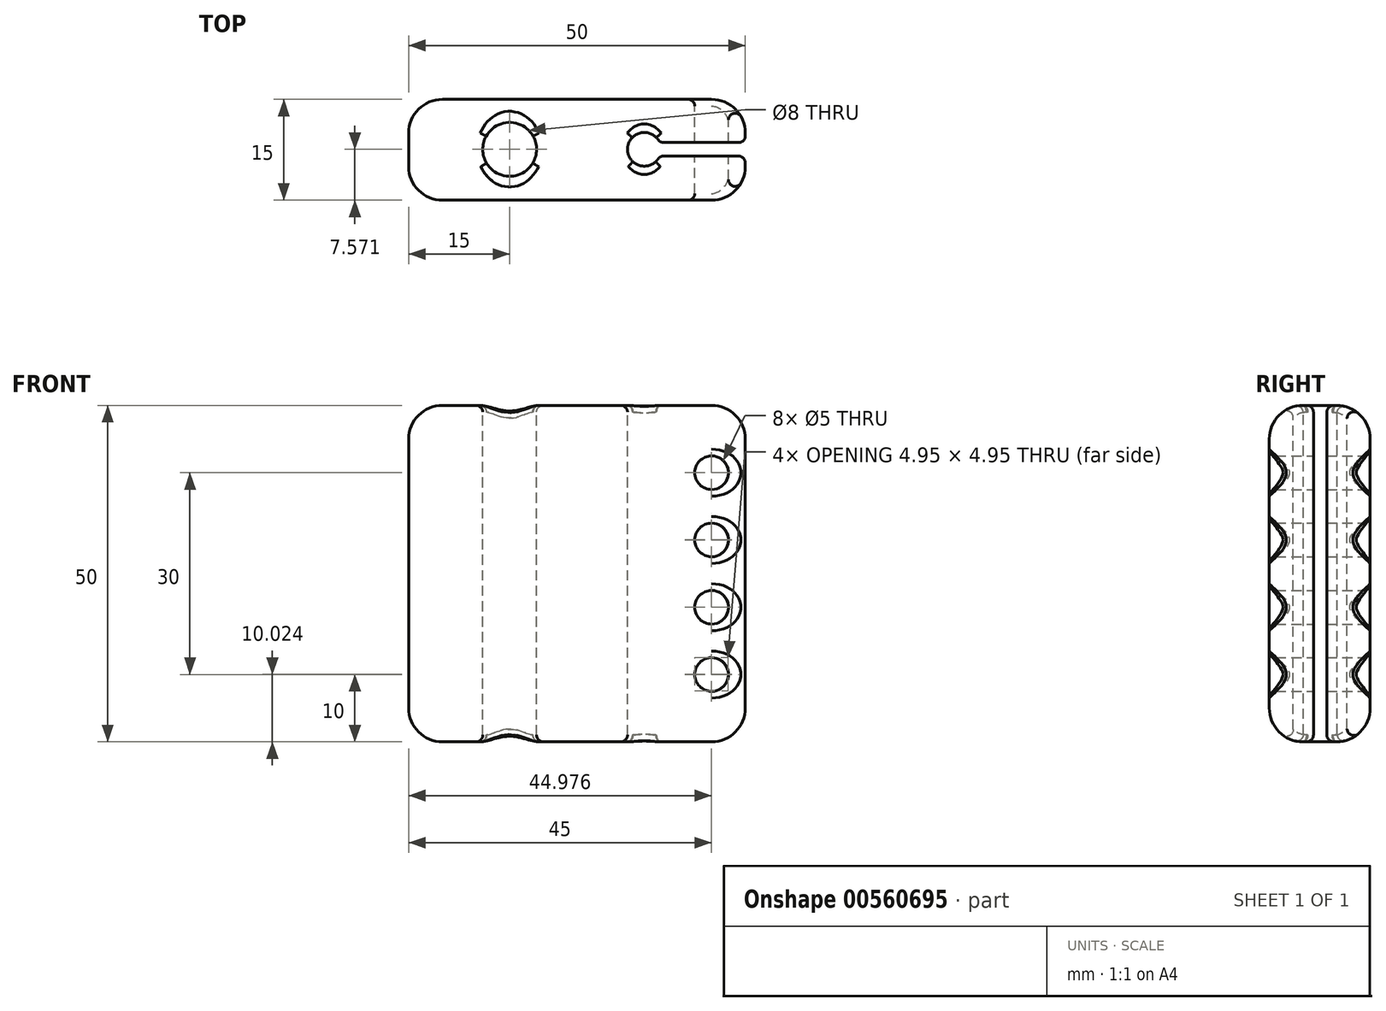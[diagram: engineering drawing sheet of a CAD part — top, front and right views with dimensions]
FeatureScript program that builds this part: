
annotation { "Feature Type Name" : "Feature", "Feature Type Description" : "" }
export const myFeature = defineFeature(function(context is Context, id is Id, definition is map)
    precondition{}
    {
        {
            var Q0;
            Q0=qCreatedBy(makeId("Front.planeOp"),FACE);
            var sketch = newSketch(context, id + "F0", { "sketchPlane" : qUnion([Q0])});
            skLineSegment(sketch, "E0.bottom", {"start": v(0, 0) * mm, "end": v(50, 0) * mm});
            skLineSegment(sketch, "E0.top", {"start": v(0, -50) * mm, "end": v(50, -50) * mm});
            skLineSegment(sketch, "E0.left", {"start": v(0, 0) * mm, "end": v(0, -50) * mm});
            skLineSegment(sketch, "E0.right", {"start": v(50, 0) * mm, "end": v(50, -50) * mm});
            skSolve(sketch);
        }
        {
            var Q0;
            Q0=makeQuery(id+"F0.imprint","IMPRINT",FACE,{"disambiguationData":[TD([[makeQuery(id+"F0.imprint","IMPRINT",EDGE,{"derivedFrom":sQuery(id+"F0.wireOp",EDGE,"E0.bottom")}),-1.0]])]});
            extrude(context, id + "F1", {"entities" : qUnion([Q0]), "depth" : 15 * mm, "offsetDistance" : 25 * mm});
        }
        {
            var Q0;
            Q0=qCreatedBy(makeId("Top.planeOp"),FACE);
            var sketch = newSketch(context, id + "F2", { "sketchPlane" : qUnion([Q0])});
            skCircle(sketch, "E1", {"center": v(35, -7.43) * mm, "radius": 2.5 * mm});
            skCircle(sketch, "E2", {"center": v(15, -7.43) * mm, "radius": 4 * mm});
            skLineSegment(sketch, "E3", {"start": v(37.5, -7.43) * mm, "end": v(68.19, -7.43) * mm, "construction": true});
            skLineSegment(sketch, "E4", {"start": v(55.03, -8.43) * mm, "end": v(55.03, -6.43) * mm});
            skLineSegment(sketch, "E5", {"start": v(55.03, -6.43) * mm, "end": v(37.3, -6.43) * mm});
            skLineSegment(sketch, "E6", {"start": v(55.03, -8.43) * mm, "end": v(37.3, -8.43) * mm});
            skSolve(sketch);
        }
        {
            var Q0;
            Q0=makeQuery(id+"F2.imprint","IMPRINT",FACE,{"disambiguationData":[TD([[makeQuery(id+"F2.imprint","IMPRINT",EDGE,{"derivedFrom":sQuery(id+"F2.wireOp",EDGE,"E1")}),1.0]])]});
            var Q1;
            Q1=makeQuery(id+"F2.imprint","IMPRINT",FACE,{"disambiguationData":[TD([[makeQuery(id+"F2.imprint","IMPRINT",EDGE,{"derivedFrom":sQuery(id+"F2.wireOp",EDGE,"E2")}),1.0]])]});
            var Q2;
            {var subQ5=sQuery(id+"F2.wireOp",EDGE,"E4");Q2=makeQuery(id+"F2.imprint","IMPRINT",FACE,{"disambiguationData":[TD([[makeQuery(id+"F2.imprint","IMPRINT",EDGE,{"derivedFrom":subQ5}),1.0]])]});}
            extrude(context, id + "F3", {"entities" : qUnion([Q0, Q1, Q2]), "operationType" : NewBodyOperationType.REMOVE, "endBound" : BoundingType.THROUGH_ALL, "oppositeDirection" : true, "depth" : 25 * mm, "offsetDistance" : 25 * mm});
        }
        {
            var Q0;
            Q0=qCreatedBy(makeId("Front.planeOp"),FACE);
            var sketch = newSketch(context, id + "F4", { "sketchPlane" : qUnion([Q0])});
            skCircle(sketch, "E7", {"center": v(45, -40) * mm, "radius": 2.5 * mm});
            skCircle(sketch, "E8", {"center": v(45, -30) * mm, "radius": 2.5 * mm});
            skCircle(sketch, "E9", {"center": v(45, -10) * mm, "radius": 2.5 * mm});
            skCircle(sketch, "E10", {"center": v(45, -20) * mm, "radius": 2.5 * mm});
            skSolve(sketch);
        }
        {
            var Q0;
            Q0 = qSketchRegion(id + "F4", true);
            extrude(context, id + "F5", {"entities" : qUnion([Q0]), "operationType" : NewBodyOperationType.REMOVE, "endBound" : BoundingType.THROUGH_ALL, "depth" : 25 * mm, "offsetDistance" : 25 * mm});
        }
        {
            var Q0;
            Q0=makeQuery(id+"F1.opExtrude","CAP_EDGE",EDGE,{"disambiguationData":[OSD([sQuery(id+"F0.wireOp",EDGE,"E0.right")])],"isStart":false});
            var Q1;
            Q1=makeQuery(id+"F1.opExtrude","CAP_EDGE",EDGE,{"disambiguationData":[OSD([sQuery(id+"F0.wireOp",EDGE,"E0.right")])],"isStart":true});
            var Q2;
            Q2=makeQuery(id+"F1.opExtrude","CAP_EDGE",EDGE,{"disambiguationData":[OSD([sQuery(id+"F0.wireOp",EDGE,"E0.left")])],"isStart":true});
            var Q3;
            Q3=makeQuery(id+"F1.opExtrude","CAP_EDGE",EDGE,{"disambiguationData":[OSD([sQuery(id+"F0.wireOp",EDGE,"E0.left")])],"isStart":false});
            var Q4;
            Q4=makeQuery(id+"F1.opExtrude","SWEPT_EDGE",EDGE,{"disambiguationData":[OSD([sQuery(id+"F0.wireOp",EDGE,"E0.top"),sQuery(id+"F0.wireOp",EDGE,"E0.left")])]});
            var Q5;
            {var subQ0=sQuery(id+"F0.wireOp",EDGE,"E0.right");var subQ1=sQuery(id+"F0.wireOp",EDGE,"E0.top");Q5=makeQuery(id+"F3.boolean.opBoolean","SPLIT",EDGE,{"disambiguationData":[TD([makeQuery(id+"F3.opExtrude","SWEPT_FACE",FACE,{"disambiguationData":[OSD([sQuery(id+"F2.wireOp",EDGE,"E5")])]})])],"derivedFrom":makeQuery(id+"F1.opExtrude","SWEPT_EDGE",EDGE,{"disambiguationData":[OSD([subQ1,subQ0])]})});}
            var Q6;
            {var subQ0=sQuery(id+"F0.wireOp",EDGE,"E0.right");var subQ1=sQuery(id+"F0.wireOp",EDGE,"E0.top");Q6=makeQuery(id+"F3.boolean.opBoolean","SPLIT",EDGE,{"disambiguationData":[TD([makeQuery(id+"F3.opExtrude","SWEPT_FACE",FACE,{"disambiguationData":[OSD([sQuery(id+"F2.wireOp",EDGE,"E6")])]})])],"derivedFrom":makeQuery(id+"F1.opExtrude","SWEPT_EDGE",EDGE,{"disambiguationData":[OSD([subQ1,subQ0])]})});}
            var Q7;
            Q7=makeQuery(id+"F1.opExtrude","SWEPT_EDGE",EDGE,{"disambiguationData":[OSD([sQuery(id+"F0.wireOp",EDGE,"E0.bottom"),sQuery(id+"F0.wireOp",EDGE,"E0.left")])]});
            var Q8;
            {var subQ0=sQuery(id+"F0.wireOp",EDGE,"E0.bottom");var subQ1=sQuery(id+"F0.wireOp",EDGE,"E0.right");Q8=makeQuery(id+"F3.boolean.opBoolean","SPLIT",EDGE,{"disambiguationData":[TD([makeQuery(id+"F3.opExtrude","SWEPT_FACE",FACE,{"disambiguationData":[OSD([sQuery(id+"F2.wireOp",EDGE,"E5")])]})])],"derivedFrom":makeQuery(id+"F1.opExtrude","SWEPT_EDGE",EDGE,{"disambiguationData":[OSD([subQ0,subQ1])]})});}
            var Q9;
            {var subQ0=sQuery(id+"F0.wireOp",EDGE,"E0.bottom");var subQ1=sQuery(id+"F0.wireOp",EDGE,"E0.right");Q9=makeQuery(id+"F3.boolean.opBoolean","SPLIT",EDGE,{"disambiguationData":[TD([makeQuery(id+"F3.opExtrude","SWEPT_FACE",FACE,{"disambiguationData":[OSD([sQuery(id+"F2.wireOp",EDGE,"E6")])]})])],"derivedFrom":makeQuery(id+"F1.opExtrude","SWEPT_EDGE",EDGE,{"disambiguationData":[OSD([subQ0,subQ1])]})});}
            var Q10;
            Q10=makeQuery(id+"F1.opExtrude","CAP_EDGE",EDGE,{"disambiguationData":[OSD([sQuery(id+"F0.wireOp",EDGE,"E0.top")])],"isStart":true});
            var Q11;
            Q11=makeQuery(id+"F1.opExtrude","CAP_EDGE",EDGE,{"disambiguationData":[OSD([sQuery(id+"F0.wireOp",EDGE,"E0.top")])],"isStart":false});
            var Q12;
            Q12=makeQuery(id+"F1.opExtrude","CAP_EDGE",EDGE,{"disambiguationData":[OSD([sQuery(id+"F0.wireOp",EDGE,"E0.bottom")])],"isStart":true});
            var Q13;
            Q13=makeQuery(id+"F1.opExtrude","CAP_EDGE",EDGE,{"disambiguationData":[OSD([sQuery(id+"F0.wireOp",EDGE,"E0.bottom")])],"isStart":false});
            fillet(context, id + "F6", {"entities" : qUnion([Q0, Q1, Q2, Q3, Q4, Q5, Q6, Q7, Q8, Q9, Q10, Q11, Q12, Q13]), "radius" : 5 * mm, "tangentPropagation" : true, "allowEdgeOverflow" : false});
        }
        {
            var Q0;
            {var subQ0=sQuery(id+"F0.wireOp",EDGE,"E0.right");Q0=makeQuery(id+"F6.opFillet","BLEND_EDGE",EDGE,{"blendedFrom":[makeQuery(id+"F1.opExtrude","CAP_EDGE",EDGE,{"disambiguationData":[OSD([subQ0])],"isStart":false}),makeQuery(id+"F5.boolean.opBoolean","COPY",FACE,{"disambiguationData":[TD([makeQuery(id+"F3.boolean.opBoolean","COPY",FACE,{"derivedFrom":makeQuery(id+"F3.opExtrude","SWEPT_FACE",FACE,{"disambiguationData":[OSD([sQuery(id+"F2.wireOp",EDGE,"E6")])]})})])],"derivedFrom":makeQuery(id+"F5.opExtrude","SWEPT_FACE",FACE,{"disambiguationData":[OSD([sQuery(id+"F4.wireOp",EDGE,"E9")])]})})],"blendedInto":[makeQuery(id+"F5.boolean.opBoolean","COPY",FACE,{"disambiguationData":[TD([makeQuery(id+"F3.boolean.opBoolean","COPY",FACE,{"derivedFrom":makeQuery(id+"F3.opExtrude","SWEPT_FACE",FACE,{"disambiguationData":[OSD([sQuery(id+"F2.wireOp",EDGE,"E6")])]})})])],"derivedFrom":makeQuery(id+"F5.opExtrude","SWEPT_FACE",FACE,{"disambiguationData":[OSD([sQuery(id+"F4.wireOp",EDGE,"E9")])]})})]});}
            var Q1;
            Q1=makeQuery(id+"F5.boolean.opBoolean","INTERSECT",EDGE,{"derivedFrom":[makeQuery(id+"F1.opExtrude","CAP_FACE",FACE,{"disambiguationData":[OSD([sQuery(id+"F0.wireOp",EDGE,"E0.bottom"),sQuery(id+"F0.wireOp",EDGE,"E0.top"),sQuery(id+"F0.wireOp",EDGE,"E0.left"),sQuery(id+"F0.wireOp",EDGE,"E0.right")])],"isStart":false}),makeQuery(id+"F5.opExtrude","SWEPT_FACE",FACE,{"disambiguationData":[OSD([sQuery(id+"F4.wireOp",EDGE,"E9")])]})]});
            var Q2;
            {var subQ0=sQuery(id+"F0.wireOp",EDGE,"E0.right");Q2=makeQuery(id+"F6.opFillet","BLEND_EDGE",EDGE,{"blendedFrom":[makeQuery(id+"F1.opExtrude","CAP_EDGE",EDGE,{"disambiguationData":[OSD([subQ0])],"isStart":false}),makeQuery(id+"F5.boolean.opBoolean","COPY",FACE,{"disambiguationData":[TD([makeQuery(id+"F3.boolean.opBoolean","COPY",FACE,{"derivedFrom":makeQuery(id+"F3.opExtrude","SWEPT_FACE",FACE,{"disambiguationData":[OSD([sQuery(id+"F2.wireOp",EDGE,"E6")])]})})])],"derivedFrom":makeQuery(id+"F5.opExtrude","SWEPT_FACE",FACE,{"disambiguationData":[OSD([sQuery(id+"F4.wireOp",EDGE,"E10")])]})})],"blendedInto":[makeQuery(id+"F5.boolean.opBoolean","COPY",FACE,{"disambiguationData":[TD([makeQuery(id+"F3.boolean.opBoolean","COPY",FACE,{"derivedFrom":makeQuery(id+"F3.opExtrude","SWEPT_FACE",FACE,{"disambiguationData":[OSD([sQuery(id+"F2.wireOp",EDGE,"E6")])]})})])],"derivedFrom":makeQuery(id+"F5.opExtrude","SWEPT_FACE",FACE,{"disambiguationData":[OSD([sQuery(id+"F4.wireOp",EDGE,"E10")])]})})]});}
            var Q3;
            {var subQ0=sQuery(id+"F0.wireOp",EDGE,"E0.right");Q3=makeQuery(id+"F6.opFillet","BLEND_EDGE",EDGE,{"blendedFrom":[makeQuery(id+"F1.opExtrude","CAP_EDGE",EDGE,{"disambiguationData":[OSD([subQ0])],"isStart":false}),makeQuery(id+"F5.boolean.opBoolean","COPY",FACE,{"disambiguationData":[TD([makeQuery(id+"F3.boolean.opBoolean","COPY",FACE,{"derivedFrom":makeQuery(id+"F3.opExtrude","SWEPT_FACE",FACE,{"disambiguationData":[OSD([sQuery(id+"F2.wireOp",EDGE,"E6")])]})})])],"derivedFrom":makeQuery(id+"F5.opExtrude","SWEPT_FACE",FACE,{"disambiguationData":[OSD([sQuery(id+"F4.wireOp",EDGE,"E8")])]})})],"blendedInto":[makeQuery(id+"F5.boolean.opBoolean","COPY",FACE,{"disambiguationData":[TD([makeQuery(id+"F3.boolean.opBoolean","COPY",FACE,{"derivedFrom":makeQuery(id+"F3.opExtrude","SWEPT_FACE",FACE,{"disambiguationData":[OSD([sQuery(id+"F2.wireOp",EDGE,"E6")])]})})])],"derivedFrom":makeQuery(id+"F5.opExtrude","SWEPT_FACE",FACE,{"disambiguationData":[OSD([sQuery(id+"F4.wireOp",EDGE,"E8")])]})})]});}
            var Q4;
            {var subQ0=sQuery(id+"F0.wireOp",EDGE,"E0.right");Q4=makeQuery(id+"F6.opFillet","BLEND_EDGE",EDGE,{"blendedFrom":[makeQuery(id+"F1.opExtrude","CAP_EDGE",EDGE,{"disambiguationData":[OSD([subQ0])],"isStart":false}),makeQuery(id+"F5.boolean.opBoolean","COPY",FACE,{"disambiguationData":[TD([makeQuery(id+"F3.boolean.opBoolean","COPY",FACE,{"derivedFrom":makeQuery(id+"F3.opExtrude","SWEPT_FACE",FACE,{"disambiguationData":[OSD([sQuery(id+"F2.wireOp",EDGE,"E6")])]})})])],"derivedFrom":makeQuery(id+"F5.opExtrude","SWEPT_FACE",FACE,{"disambiguationData":[OSD([sQuery(id+"F4.wireOp",EDGE,"E7")])]})})],"blendedInto":[makeQuery(id+"F5.boolean.opBoolean","COPY",FACE,{"disambiguationData":[TD([makeQuery(id+"F3.boolean.opBoolean","COPY",FACE,{"derivedFrom":makeQuery(id+"F3.opExtrude","SWEPT_FACE",FACE,{"disambiguationData":[OSD([sQuery(id+"F2.wireOp",EDGE,"E6")])]})})])],"derivedFrom":makeQuery(id+"F5.opExtrude","SWEPT_FACE",FACE,{"disambiguationData":[OSD([sQuery(id+"F4.wireOp",EDGE,"E7")])]})})]});}
            var Q5;
            {var subQ0=sQuery(id+"F0.wireOp",EDGE,"E0.right");Q5=makeQuery(id+"F6.opFillet","BLEND_EDGE",EDGE,{"blendedFrom":[makeQuery(id+"F1.opExtrude","CAP_EDGE",EDGE,{"disambiguationData":[OSD([subQ0])],"isStart":true}),makeQuery(id+"F5.boolean.opBoolean","COPY",FACE,{"disambiguationData":[TD([makeQuery(id+"F3.boolean.opBoolean","COPY",FACE,{"derivedFrom":makeQuery(id+"F3.opExtrude","SWEPT_FACE",FACE,{"disambiguationData":[OSD([sQuery(id+"F2.wireOp",EDGE,"E5")])]})})])],"derivedFrom":makeQuery(id+"F5.opExtrude","SWEPT_FACE",FACE,{"disambiguationData":[OSD([sQuery(id+"F4.wireOp",EDGE,"E9")])]})})],"blendedInto":[makeQuery(id+"F5.boolean.opBoolean","COPY",FACE,{"disambiguationData":[TD([makeQuery(id+"F3.boolean.opBoolean","COPY",FACE,{"derivedFrom":makeQuery(id+"F3.opExtrude","SWEPT_FACE",FACE,{"disambiguationData":[OSD([sQuery(id+"F2.wireOp",EDGE,"E5")])]})})])],"derivedFrom":makeQuery(id+"F5.opExtrude","SWEPT_FACE",FACE,{"disambiguationData":[OSD([sQuery(id+"F4.wireOp",EDGE,"E9")])]})})]});}
            var Q6;
            {var subQ0=sQuery(id+"F0.wireOp",EDGE,"E0.right");Q6=makeQuery(id+"F6.opFillet","BLEND_EDGE",EDGE,{"blendedFrom":[makeQuery(id+"F1.opExtrude","CAP_EDGE",EDGE,{"disambiguationData":[OSD([subQ0])],"isStart":true}),makeQuery(id+"F5.boolean.opBoolean","COPY",FACE,{"disambiguationData":[TD([makeQuery(id+"F3.boolean.opBoolean","COPY",FACE,{"derivedFrom":makeQuery(id+"F3.opExtrude","SWEPT_FACE",FACE,{"disambiguationData":[OSD([sQuery(id+"F2.wireOp",EDGE,"E5")])]})})])],"derivedFrom":makeQuery(id+"F5.opExtrude","SWEPT_FACE",FACE,{"disambiguationData":[OSD([sQuery(id+"F4.wireOp",EDGE,"E10")])]})})],"blendedInto":[makeQuery(id+"F5.boolean.opBoolean","COPY",FACE,{"disambiguationData":[TD([makeQuery(id+"F3.boolean.opBoolean","COPY",FACE,{"derivedFrom":makeQuery(id+"F3.opExtrude","SWEPT_FACE",FACE,{"disambiguationData":[OSD([sQuery(id+"F2.wireOp",EDGE,"E5")])]})})])],"derivedFrom":makeQuery(id+"F5.opExtrude","SWEPT_FACE",FACE,{"disambiguationData":[OSD([sQuery(id+"F4.wireOp",EDGE,"E10")])]})})]});}
            var Q7;
            {var subQ0=sQuery(id+"F0.wireOp",EDGE,"E0.right");Q7=makeQuery(id+"F6.opFillet","BLEND_EDGE",EDGE,{"blendedFrom":[makeQuery(id+"F1.opExtrude","CAP_EDGE",EDGE,{"disambiguationData":[OSD([subQ0])],"isStart":true}),makeQuery(id+"F5.boolean.opBoolean","COPY",FACE,{"disambiguationData":[TD([makeQuery(id+"F3.boolean.opBoolean","COPY",FACE,{"derivedFrom":makeQuery(id+"F3.opExtrude","SWEPT_FACE",FACE,{"disambiguationData":[OSD([sQuery(id+"F2.wireOp",EDGE,"E5")])]})})])],"derivedFrom":makeQuery(id+"F5.opExtrude","SWEPT_FACE",FACE,{"disambiguationData":[OSD([sQuery(id+"F4.wireOp",EDGE,"E8")])]})})],"blendedInto":[makeQuery(id+"F5.boolean.opBoolean","COPY",FACE,{"disambiguationData":[TD([makeQuery(id+"F3.boolean.opBoolean","COPY",FACE,{"derivedFrom":makeQuery(id+"F3.opExtrude","SWEPT_FACE",FACE,{"disambiguationData":[OSD([sQuery(id+"F2.wireOp",EDGE,"E5")])]})})])],"derivedFrom":makeQuery(id+"F5.opExtrude","SWEPT_FACE",FACE,{"disambiguationData":[OSD([sQuery(id+"F4.wireOp",EDGE,"E8")])]})})]});}
            var Q8;
            {var subQ0=sQuery(id+"F0.wireOp",EDGE,"E0.right");Q8=makeQuery(id+"F6.opFillet","BLEND_EDGE",EDGE,{"blendedFrom":[makeQuery(id+"F1.opExtrude","CAP_EDGE",EDGE,{"disambiguationData":[OSD([subQ0])],"isStart":true}),makeQuery(id+"F5.boolean.opBoolean","COPY",FACE,{"disambiguationData":[TD([makeQuery(id+"F3.boolean.opBoolean","COPY",FACE,{"derivedFrom":makeQuery(id+"F3.opExtrude","SWEPT_FACE",FACE,{"disambiguationData":[OSD([sQuery(id+"F2.wireOp",EDGE,"E5")])]})})])],"derivedFrom":makeQuery(id+"F5.opExtrude","SWEPT_FACE",FACE,{"disambiguationData":[OSD([sQuery(id+"F4.wireOp",EDGE,"E7")])]})})],"blendedInto":[makeQuery(id+"F5.boolean.opBoolean","COPY",FACE,{"disambiguationData":[TD([makeQuery(id+"F3.boolean.opBoolean","COPY",FACE,{"derivedFrom":makeQuery(id+"F3.opExtrude","SWEPT_FACE",FACE,{"disambiguationData":[OSD([sQuery(id+"F2.wireOp",EDGE,"E5")])]})})])],"derivedFrom":makeQuery(id+"F5.opExtrude","SWEPT_FACE",FACE,{"disambiguationData":[OSD([sQuery(id+"F4.wireOp",EDGE,"E7")])]})})]});}
            var Q9;
            Q9=makeQuery(id+"F3.boolean.opBoolean","INTERSECT",EDGE,{"derivedFrom":[makeQuery(id+"F1.opExtrude","SWEPT_FACE",FACE,{"disambiguationData":[OSD([sQuery(id+"F0.wireOp",EDGE,"E0.top")])]}),makeQuery(id+"F3.opExtrude","SWEPT_FACE",FACE,{"disambiguationData":[OSD([sQuery(id+"F2.wireOp",EDGE,"E1")])]})]});
            var Q10;
            Q10=makeQuery(id+"F3.boolean.opBoolean","COPY",FACE,{"derivedFrom":makeQuery(id+"F3.opExtrude","SWEPT_FACE",FACE,{"disambiguationData":[OSD([sQuery(id+"F2.wireOp",EDGE,"E2")])]})});
            var Q11;
            Q11=makeQuery(id+"F3.boolean.opBoolean","COPY",FACE,{"derivedFrom":makeQuery(id+"F3.opExtrude","SWEPT_FACE",FACE,{"disambiguationData":[OSD([sQuery(id+"F2.wireOp",EDGE,"E1")])]})});
            var Q12;
            Q12=makeQuery(id+"F3.boolean.opBoolean","INTERSECT",EDGE,{"derivedFrom":[makeQuery(id+"F1.opExtrude","SWEPT_FACE",FACE,{"disambiguationData":[OSD([sQuery(id+"F0.wireOp",EDGE,"E0.top")])]}),makeQuery(id+"F3.opExtrude","SWEPT_FACE",FACE,{"disambiguationData":[OSD([sQuery(id+"F2.wireOp",EDGE,"E6")])]})]});
            var Q13;
            Q13=makeQuery(id+"F3.boolean.opBoolean","INTERSECT",EDGE,{"derivedFrom":[makeQuery(id+"F1.opExtrude","SWEPT_FACE",FACE,{"disambiguationData":[OSD([sQuery(id+"F0.wireOp",EDGE,"E0.top")])]}),makeQuery(id+"F3.opExtrude","SWEPT_FACE",FACE,{"disambiguationData":[OSD([sQuery(id+"F2.wireOp",EDGE,"E5")])]})]});
            var Q14;
            {var subQ0=makeQuery(id+"F3.opExtrude","SWEPT_FACE",FACE,{"disambiguationData":[OSD([sQuery(id+"F2.wireOp",EDGE,"E6")])]});var subQ1=sQuery(id+"F0.wireOp",EDGE,"E0.right");var subQ2=sQuery(id+"F0.wireOp",EDGE,"E0.top");Q14=makeQuery(id+"F6.opFillet","BLEND_EDGE",EDGE,{"blendedFrom":[makeQuery(id+"F3.boolean.opBoolean","SPLIT",EDGE,{"disambiguationData":[TD([subQ0])],"derivedFrom":makeQuery(id+"F1.opExtrude","SWEPT_EDGE",EDGE,{"disambiguationData":[OSD([subQ2,subQ1])]})}),makeQuery(id+"F3.boolean.opBoolean","COPY",FACE,{"derivedFrom":subQ0})],"blendedInto":[makeQuery(id+"F3.boolean.opBoolean","COPY",FACE,{"derivedFrom":subQ0})]});}
            var Q15;
            {var subQ0=makeQuery(id+"F3.opExtrude","SWEPT_FACE",FACE,{"disambiguationData":[OSD([sQuery(id+"F2.wireOp",EDGE,"E5")])]});var subQ1=sQuery(id+"F0.wireOp",EDGE,"E0.right");var subQ2=sQuery(id+"F0.wireOp",EDGE,"E0.top");Q15=makeQuery(id+"F6.opFillet","BLEND_EDGE",EDGE,{"blendedFrom":[makeQuery(id+"F3.boolean.opBoolean","SPLIT",EDGE,{"disambiguationData":[TD([subQ0])],"derivedFrom":makeQuery(id+"F1.opExtrude","SWEPT_EDGE",EDGE,{"disambiguationData":[OSD([subQ2,subQ1])]})}),makeQuery(id+"F3.boolean.opBoolean","COPY",FACE,{"derivedFrom":subQ0})],"blendedInto":[makeQuery(id+"F3.boolean.opBoolean","COPY",FACE,{"derivedFrom":subQ0})]});}
            fillet(context, id + "F7", {"entities" : qUnion([Q0, Q1, Q2, Q3, Q4, Q5, Q6, Q7, Q8, Q9, Q10, Q11, Q12, Q13, Q14, Q15]), "radius" : 1 * mm, "tangentPropagation" : true, "allowEdgeOverflow" : false});
        }
    });
